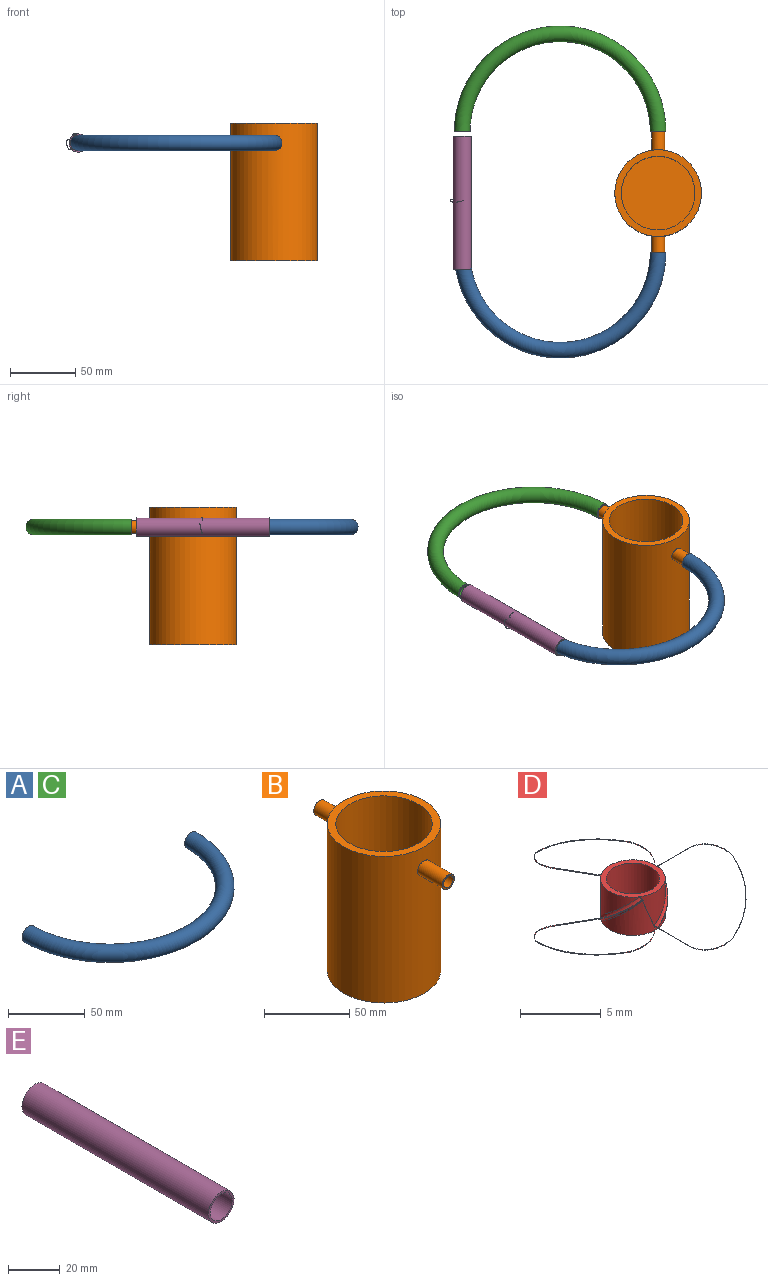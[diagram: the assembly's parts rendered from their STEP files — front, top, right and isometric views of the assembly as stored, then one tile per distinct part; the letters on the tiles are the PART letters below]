
ASSEMBLY  parts=5 mates=4
PART A: 4 faces, bbox 175.3x87.7x12 mm
  f0: torus R=75mm, axis (0,0,-1), area 8882.6mm2, adj f1,f2
  f1: plane 12x12mm, normal (0,1,0), area 34.6mm2, adj f0,f3
  f2: plane 12x12mm, normal (0,1,0), area 34.6mm2, adj f0,f3
  f3: torus R=75mm, axis (0,0,-1), area 7402.2mm2, adj f1,f2
PART B: 13 faces, bbox 66.4x106.4x105 mm
  f0: cylinder r=33.2mm len=105mm, axis (0,0,-1), area 21746.5mm2, adj f2,f3,f6,f10
  f1: cylinder r=4mm len=20.24mm, axis (0,1,0), area 505.7mm2, adj f7,f8
  f2: plane 66.4x66.4mm, normal (0,0,1), area 964.5mm2, adj f0,f4
  f3: plane 66.4x66.4mm, normal (0,0,-1), area 3462.8mm2, adj f0
  f4: cylinder r=28.2mm len=100mm, axis (0,0,-1), area 17718.6mm2, adj f2,f5
  f5: plane 56.4x56.4mm, normal (0,0,1), area 2498.3mm2, adj f4
  f6: cylinder r=5mm len=20.38mm, axis (0,-1,0), area 634.2mm2, adj f0,f7
  f7: plane 10x10mm, normal (0,1,0), area 28.3mm2, adj f1,f6
  f8: cylinder r=33.2mm len=8mm, axis (0,0,-1), area 50.4mm2, adj f1
  f9: cylinder r=4mm len=20.24mm, axis (0,-1,0), area 505.7mm2, adj f11,f12
  f10: cylinder r=5mm len=20.38mm, axis (0,1,0), area 634.2mm2, adj f0,f11
  f11: plane 10x10mm, normal (0,-1,0), area 28.3mm2, adj f9,f10
  f12: cylinder r=33.2mm len=8mm, axis (0,0,-1), area 50.4mm2, adj f9
PART C: same geometry as A
PART D: 29 faces, bbox 14.4x14.4x3.1 mm
  f0: cylinder r=2mm len=4mm, axis (0,0,-1), area 28.4mm2, adj f1,f3,f4,f5,f7,f8,f10,f13
  f1: cylinder r=2mm len=2.56mm, axis (0,0,-1), area 3.3mm2, adj f0,f3,f18
  f2: cylinder r=1.65mm len=3.3mm, axis (0,0,-1), area 30.1mm2, adj f3,f4
  f3: plane 4x4mm, normal (0,0,1), area 4mm2, adj f0,f1,f2,f9,f17,f25
  f4: plane 4x4mm, normal (0,0,-1), area 4mm2, adj f0,f2
  f5: bspline ~5.05x0.38mm, area 0.2mm2, adj f0,f8,f10,f11
  f6: bspline ~4.53x4.53mm, area 0.3mm2, adj f11,f12
  f7: bspline ~5.05x0.38mm, area 0.2mm2, adj f0,f8,f9,f12
  f8: bspline ~2.96x2.46mm, area 1.1mm2, adj f0,f5,f7
  f9: bspline ~0.18x0.17mm, area 0mm2, adj f3,f7,f10
  f10: bspline ~2.96x2.53mm, area 1.1mm2, adj f0,f5,f9
  f11: bspline ~2.39x2.29mm, area 0.2mm2, adj f5,f6
  f12: bspline ~2.39x2.29mm, area 0.2mm2, adj f6,f7
  f13: bspline ~4.46x2.67mm, area 0.2mm2, adj f0,f16,f18,f19
  f14: bspline ~6.04x1.76mm, area 0.3mm2, adj f19,f20
  f15: bspline ~4.46x2.67mm, area 0.2mm2, adj f0,f16,f17,f20
  f16: bspline ~3.26x2.96mm, area 1.1mm2, adj f0,f13,f15
  f17: bspline ~0.23x0.16mm, area 0mm2, adj f3,f15,f18
  f18: bspline ~3.28x2.96mm, area 1.1mm2, adj f0,f1,f13,f17
  f19: bspline ~2.55x2.27mm, area 0.2mm2, adj f13,f14
  f20: bspline ~2.8x2.05mm, area 0.2mm2, adj f14,f15
  f21: bspline ~4.46x2.67mm, area 0.2mm2, adj f0,f24,f26,f27
  f22: bspline ~6.04x1.76mm, area 0.3mm2, adj f27,f28
  f23: bspline ~4.46x2.67mm, area 0.2mm2, adj f0,f24,f25,f28
  f24: bspline ~3.25x2.96mm, area 1.1mm2, adj f0,f21,f23
  f25: bspline ~0.23x0.17mm, area 0mm2, adj f3,f23,f26
  f26: bspline ~3.23x2.96mm, area 1.1mm2, adj f0,f21,f25
  f27: bspline ~2.8x2.05mm, area 0.2mm2, adj f21,f22
  f28: bspline ~2.55x2.27mm, area 0.2mm2, adj f22,f23
PART E: 4 faces, bbox 14x102x14 mm
  f0: cylinder r=6mm len=102mm, axis (0,1,0), area 3845.3mm2, adj f2,f3
  f1: cylinder r=7mm len=102mm, axis (0,1,0), area 4486.2mm2, adj f2,f3
  f2: plane 14x14mm, normal (0,-1,0), area 40.8mm2, adj f0,f1
  f3: plane 14x14mm, normal (0,1,0), area 40.8mm2, adj f0,f1
PLACE A t=(-181.38,-95.46,15.02)mm
PLACE B t=(-31.38,-50.19,-69.98)mm
PLACE C rot(axis=(1,0,0),180deg) t=(-181.38,-3.18,15.02)mm
PLACE D rot(axis=(1,0,0),90deg) t=(-183.38,-54.97,15.14)mm
PLACE E t=(-181.38,-6.62,15.02)mm
MATE slider E.f0 <-> C.f2  axis (0,1,0) through (-181.38,-6.62,15.02)mm
MATE slider C.f1 <-> B.f1  axis (0,-1,0) through (-31.38,-3.18,15.02)mm
MATE revolute D.f3 <-> E.f0  axis (0,-1,0) through (-181.38,-57.62,15.02)mm
MATE slider A.f1 <-> B.f10  axis (0,1,0) through (-31.38,-95.46,15.02)mm
